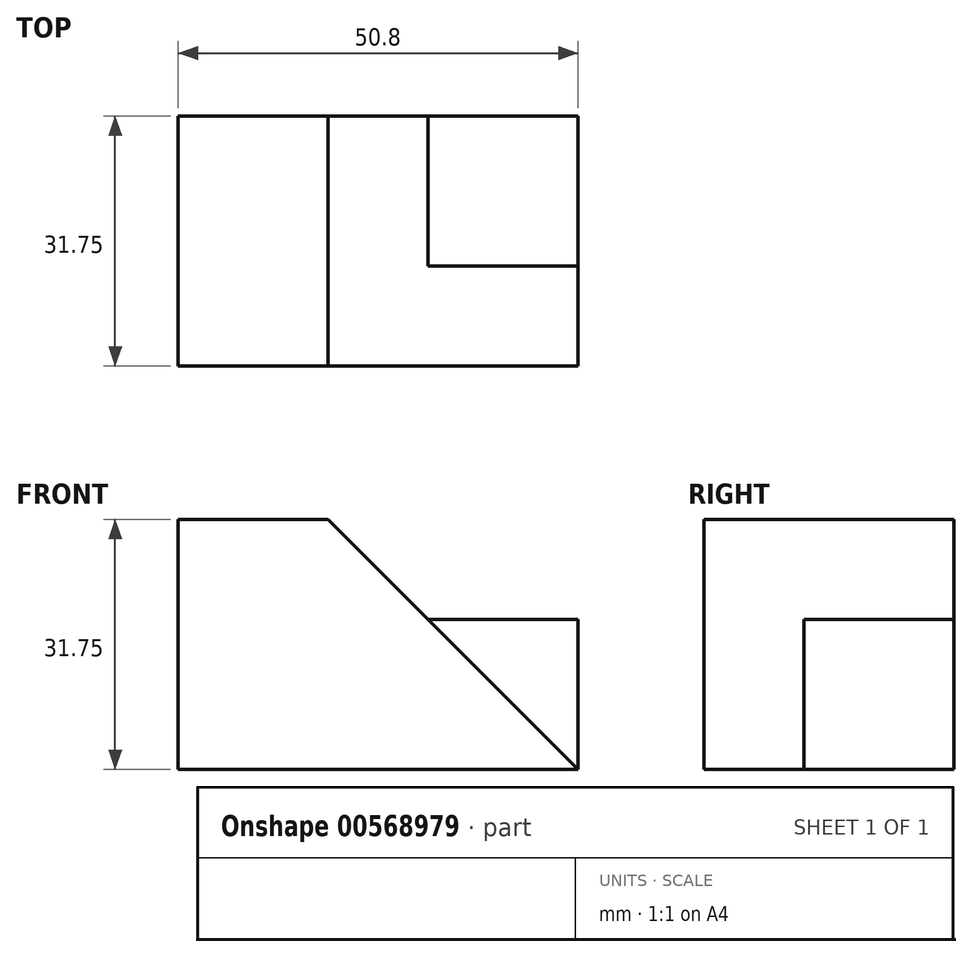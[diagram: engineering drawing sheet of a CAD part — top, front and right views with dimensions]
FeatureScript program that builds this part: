
annotation { "Feature Type Name" : "Feature", "Feature Type Description" : "" }
export const myFeature = defineFeature(function(context is Context, id is Id, definition is map)
    precondition{}
    {
        {
            var Q0;
            Q0=qCreatedBy(makeId("Front.planeOp"),FACE);
            var sketch = newSketch(context, id + "F0", { "sketchPlane" : qUnion([Q0])});
            skLineSegment(sketch, "E0.bottom", {"start": v(-21.94, 31.75) * mm, "end": v(28.86, 31.75) * mm});
            skLineSegment(sketch, "E0.top", {"start": v(-21.94, 0) * mm, "end": v(28.86, 0) * mm});
            skLineSegment(sketch, "E0.left", {"start": v(-21.94, 31.75) * mm, "end": v(-21.94, 0) * mm});
            skLineSegment(sketch, "E0.right", {"start": v(28.86, 31.75) * mm, "end": v(28.86, 0) * mm});
            skSolve(sketch);
        }
        {
            var Q0;
            Q0 = qSketchRegion(id + "F0", true);
            extrude(context, id + "F1", {"entities" : qUnion([Q0]), "depth" : 31.75 * mm, "offsetDistance" : 25.4 * mm});
        }
        {
            var Q0;
            Q0=makeQuery(id+"F1.opExtrude","CAP_FACE",FACE,{"disambiguationData":[OSD([sQuery(id+"F0.wireOp",EDGE,"E0.bottom"),sQuery(id+"F0.wireOp",EDGE,"E0.top"),sQuery(id+"F0.wireOp",EDGE,"E0.left"),sQuery(id+"F0.wireOp",EDGE,"E0.right")])],"isStart":false});
            var sketch = newSketch(context, id + "F2", { "sketchPlane" : qUnion([Q0])});
            skLineSegment(sketch, "E1", {"start": v(-2.9, 31.75) * mm, "end": v(28.86, 0) * mm});
            skLineSegment(sketch, "E2", {"start": v(28.86, 0) * mm, "end": v(28.86, 31.75) * mm});
            skLineSegment(sketch, "E3", {"start": v(28.86, 31.75) * mm, "end": v(-2.9, 31.75) * mm});
            skSolve(sketch);
        }
        {
            var Q0;
            Q0 = qSketchRegion(id + "F2", true);
            extrude(context, id + "F3", {"entities" : qUnion([Q0]), "operationType" : NewBodyOperationType.REMOVE, "oppositeDirection" : true, "depth" : 12.7 * mm, "offsetDistance" : 25.4 * mm});
        }
        {
            var Q0;
            Q0=makeQuery(id+"F1.opExtrude","CAP_FACE",FACE,{"disambiguationData":[OSD([sQuery(id+"F0.wireOp",EDGE,"E0.bottom"),sQuery(id+"F0.wireOp",EDGE,"E0.top"),sQuery(id+"F0.wireOp",EDGE,"E0.left"),sQuery(id+"F0.wireOp",EDGE,"E0.right")])],"isStart":true});
            var sketch = newSketch(context, id + "F4", { "sketchPlane" : qUnion([Q0])});
            skLineSegment(sketch, "E4", {"start": v(2.9, 31.75) * mm, "end": v(-9.8, 19.05) * mm});
            skLineSegment(sketch, "E5", {"start": v(-9.8, 19.05) * mm, "end": v(-28.86, 19.05) * mm});
            skLineSegment(sketch, "E6", {"start": v(-28.86, 19.05) * mm, "end": v(-28.86, 31.75) * mm});
            skLineSegment(sketch, "E7", {"start": v(-28.86, 31.75) * mm, "end": v(2.9, 31.75) * mm});
            skSolve(sketch);
        }
        {
            var Q0;
            Q0=makeQuery(id+"F4.imprint","IMPRINT",FACE,{"disambiguationData":[TD([[makeQuery(id+"F4.imprint","IMPRINT",EDGE,{"derivedFrom":sQuery(id+"F4.wireOp",EDGE,"E4")}),-1.0]])]});
            extrude(context, id + "F5", {"entities" : qUnion([Q0]), "operationType" : NewBodyOperationType.REMOVE, "oppositeDirection" : true, "depth" : 19.05 * mm, "offsetDistance" : 25.4 * mm});
        }
    });
